FCSTD DOCUMENT  (FreeCAD 0.20RUnknown)
Label: plate-3inch-2x3
License: All rights reserved
LicenseURL: http://en.wikipedia.org/wiki/All_rights_reserved
objects: Sketcher::SketchObject×1, PartDesign::Body×1
note: 2 computed .brp shape members not serialized (recipe doc carries the construction recipe); baked Part::Feature solids carry a one-line shape summary decoded from their .brp

FEATURE [Sketcher::SketchObject] Sketch
  FullyConstrained = false
  MapMode = 5
  Support = -> [XY_Plane]
  sketch-geometry (16):
    g0: Circle CenterX=-57.3748 CenterY=33.6716 CenterZ=0 NormalX=0 NormalY=0 NormalZ=1 AngleXU=0 Radius=12.725
    g1: Circle CenterX=94.3052 CenterY=33.6716 CenterZ=0 NormalX=0 NormalY=0 NormalZ=1 AngleXU=0 Radius=12.725
    g2: Circle CenterX=-57.3748 CenterY=-41.8084 CenterZ=0 NormalX=0 NormalY=0 NormalZ=1 AngleXU=0 Radius=12.725
    g3: Circle CenterX=94.3052 CenterY=-41.8084 CenterZ=0 NormalX=0 NormalY=0 NormalZ=1 AngleXU=0 Radius=12.725
    g4: ArcOfCircle CenterX=-92.9348 CenterY=69.2316 CenterZ=0 NormalX=0 NormalY=0 NormalZ=1 AngleXU=0 Radius=2.54 StartAngle=1.5708 EndAngle=3.14159
    g5: LineSegment StartX=-92.9348 StartY=71.7716 StartZ=0 EndX=129.865 EndY=71.7716 EndZ=0
    g6: ArcOfCircle CenterX=129.865 CenterY=69.2316 CenterZ=0 NormalX=0 NormalY=0 NormalZ=1 AngleXU=0 Radius=2.54 StartAngle=7e-16 EndAngle=1.5708
    g7: LineSegment StartX=132.405 StartY=69.2316 StartZ=0 EndX=132.405 EndY=-77.3684 EndZ=0
    g8: ArcOfCircle CenterX=129.865 CenterY=-77.3684 CenterZ=0 NormalX=0 NormalY=0 NormalZ=1 AngleXU=0 Radius=2.54 StartAngle=4.71239 EndAngle=6.28319
    g9: LineSegment StartX=129.865 StartY=-79.9084 StartZ=0 EndX=-92.9348 EndY=-79.9084 EndZ=0
    g10: ArcOfCircle CenterX=-92.9348 CenterY=-77.3684 CenterZ=0 NormalX=0 NormalY=0 NormalZ=1 AngleXU=0 Radius=2.54 StartAngle=3.14159 EndAngle=4.71239
    g11: LineSegment StartX=-95.4748 StartY=-77.3684 StartZ=0 EndX=-95.4748 EndY=69.2316 EndZ=0
    g12: GeomPoint X=-95.4748 Y=71.7716 Z=0
    g13: GeomPoint X=132.405 Y=-79.9084 Z=0
    g14: Circle CenterX=18.1052 CenterY=-41.8084 CenterZ=0 NormalX=0 NormalY=0 NormalZ=1 AngleXU=0 Radius=12.725
    g15: Circle CenterX=18.1052 CenterY=33.6716 CenterZ=0 NormalX=0 NormalY=0 NormalZ=1 AngleXU=0 Radius=12.725
  constraints (40):
    c: Diameter(g3) = 25.45
    c: Diameter(g2) = 25.45
    c: Diameter(g0) = 25.45
    c: Diameter(g1) = 25.45
    c: Tangent(g4,g5) = 1.5708
    c: Tangent(g5,g6) = 1.5708
    c: Tangent(g6,g7) = 1.5708
    c: Tangent(g7,g8) = 1.5708
    c: Tangent(g8,g9) = 1.5708
    c: Tangent(g9,g10) = 1.5708
    c: Tangent(g10,g11) = 1.5708
    c: Tangent(g11,g4) = 1.5708
    c: Horizontal(g5)
    c: Horizontal(g9)
    c: Vertical(g7)
    c: Vertical(g11)
    c: Equal(g4,g6)
    c: Equal(g6,g8)
    c: Equal(g8,g10)
    c: PointOnObject(g12,g5)
    c: PointOnObject(g12,g11)
    c: PointOnObject(g13,g7)
    c: PointOnObject(g13,g9)
    c: Diameter(g4) = 5.08
    c: Distance(g7) = 146.6
    c: Distance(g5) = 222.8
    c: Distance(g0,g11) = 38.1
    c: Distance(g0,g5) = 38.1
    c: Distance(g1,g5) = 38.1
    c: Distance(g1,g7) = 38.1
    c: Distance(g2,g9) = 38.1
    c: Distance(g2,g11) = 38.1
    c: Distance(g3,g9) = 38.1
    c: Distance(g3,g7) = 38.1
    c: Distance(g15,g5) = 38.1
    c: Distance(g14,g9) = 38.1
    c: Distance(g15,g7) = 114.3
    c: Distance(g14,g7) = 114.3
    c: Diameter(g15) = 25.45
    c: Diameter(g14) = 25.45
FEATURE [PartDesign::Body] Body
  Group = -> [Sketch]
  Origin = -> Origin
